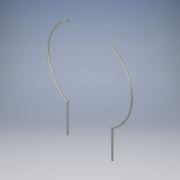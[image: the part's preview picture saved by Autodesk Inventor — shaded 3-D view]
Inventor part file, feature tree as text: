
AUTODESK INVENTOR PART (.ipt)
format: ipt  version: 2017 (Build 210142000, 142)  size: 139,264 bytes
history: native  units: in
note: dims shown in document units (in); Inventor stores cm internally (conversion verified against a paired STEP export)
features: sketch x7, plane x5, sweep x2, extrude x2
ambient origin geometry x8: Origin, YZ Plane, XZ Plane, XY Plane, X Axis, Y Axis, Z Axis, Center Point
bodies: Solid1 (feature_tree)
feature tree (16):
  sketch  "Sketch1"  dims[d3=0.25in d4=0.25in]
  plane  "Work Plane5"
  plane  "Work Plane6"
  sketch  "Sketch4"  dims[d5=0.0in d6=0.0in d7=0.0in d8=0.0in]
  sketch  "Sketch5"  dims[d9=5.0in d10=5.0in]
  sweep  "Sweep1"
  sweep  "Sweep2"
  plane  "Work Plane7"
  sketch  "Sketch6"  dims[d11=0.25in d12=5.0in d13=0.0in]
  sketch  "Sketch7"  dims[d14=5.0in]
  plane  "Work Plane8"
  extrude  "Extrusion1"  Depth=5.0in
  plane  "Work Plane10"
  extrude  "Extrusion2"  Depth=5.0in TaperAngle=0.0deg
  sketch  "Sketch8"  dims[d15=0.25in]
  sketch  "Sketch9"  dims[d16=5.0in d17=0.0in]
